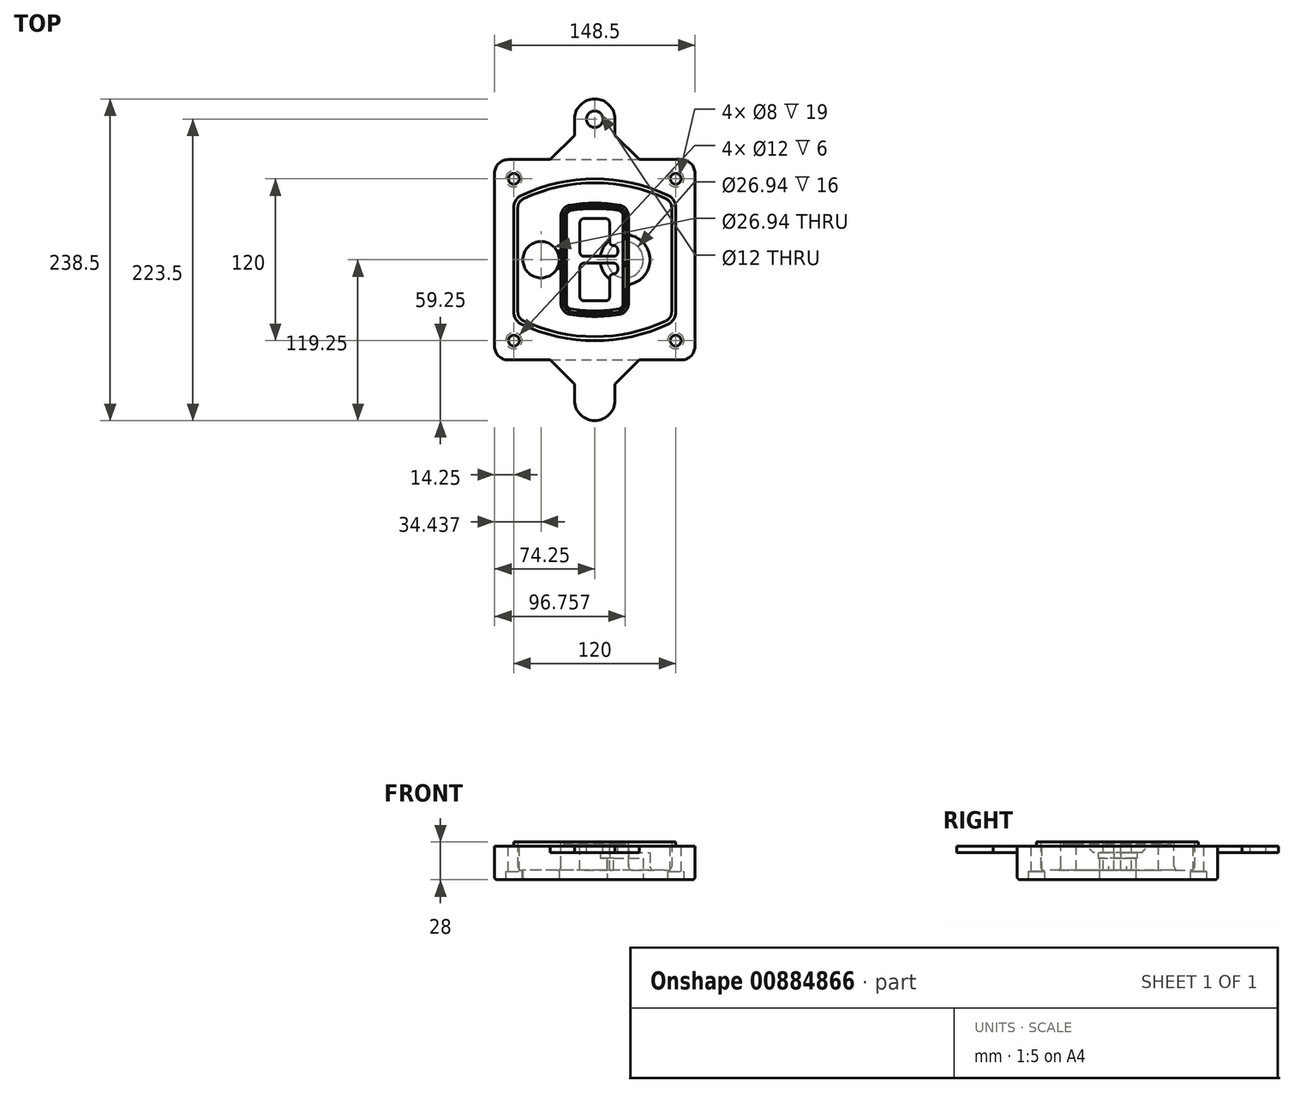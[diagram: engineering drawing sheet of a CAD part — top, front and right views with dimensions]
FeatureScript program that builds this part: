
annotation { "Feature Type Name" : "Feature", "Feature Type Description" : "" }
export const myFeature = defineFeature(function(context is Context, id is Id, definition is map)
    precondition{}
    {
        {
            var Q0;
            Q0=qCreatedBy(makeId("Top.planeOp"),FACE);
            var sketch = newSketch(context, id + "F0", { "sketchPlane" : qUnion([Q0])});
            skPoint(sketch, "E0.rect.middle", {"position": v(0, 0) * mm});
            skLineSegment(sketch, "E1.bottom", {"start": v(-64.25, -74.25) * mm, "end": v(64.25, -74.25) * mm});
            skLineSegment(sketch, "E1.top", {"start": v(-64.25, 74.25) * mm, "end": v(64.25, 74.25) * mm});
            skLineSegment(sketch, "E1.left", {"start": v(-74.25, -64.25) * mm, "end": v(-74.25, 64.25) * mm});
            skLineSegment(sketch, "E1.right", {"start": v(74.25, -64.25) * mm, "end": v(74.25, 64.25) * mm});
            skLineSegment(sketch, "E2", {"start": v(-74.25, 74.25) * mm, "end": v(74.25, -74.25) * mm, "construction": true});
            skLineSegment(sketch, "E3", {"start": v(74.25, 74.25) * mm, "end": v(-74.25, -74.25) * mm, "construction": true});
            skCircle(sketch, "E4", {"center": v(-60, 60) * mm, "radius": 4 * mm});
            skCircle(sketch, "E5", {"center": v(60, 60) * mm, "radius": 4 * mm});
            skCircle(sketch, "E6", {"center": v(60, -60) * mm, "radius": 4 * mm});
            skCircle(sketch, "E7", {"center": v(-60, -60) * mm, "radius": 4 * mm});
            skLineSegment(sketch, "E8", {"start": v(-60, 60) * mm, "end": v(60, 60) * mm, "construction": true});
            skLineSegment(sketch, "E9", {"start": v(60, 60) * mm, "end": v(60, -60) * mm, "construction": true});
            skLineSegment(sketch, "E10", {"start": v(60, -60) * mm, "end": v(-60, -60) * mm, "construction": true});
            skLineSegment(sketch, "E11", {"start": v(-60, -60) * mm, "end": v(-60, 60) * mm, "construction": true});
            skLineSegment(sketch, "E12", {"start": v(-60, 38.83) * mm, "end": v(-60, -38.83) * mm});
            skLineSegment(sketch, "E13", {"start": v(60, 38.83) * mm, "end": v(60, -38.83) * mm});
            skArc(sketch, "E14", {"start": v(54.26, 47.88) * mm, "mid": v(0, 60) * mm, "end": v(-54.26, 47.88) * mm});
            skArc(sketch, "E15", {"start": v(-54.26, -47.88) * mm, "mid": v(0, -60) * mm, "end": v(54.26, -47.88) * mm});
            skLineSegment(sketch, "E16", {"start": v(-60, 0) * mm, "end": v(60, 0) * mm, "construction": true});
            skPoint(sketch, "E17.visualSharp", {"position": v(-60, -45) * mm});
            skArc(sketch, "E17.filletArc", {"start": v(-60, -38.83) * mm, "mid": v(-58.44, -44.2) * mm, "end": v(-54.26, -47.88) * mm});
            skPoint(sketch, "E18.visualSharp", {"position": v(-60, 45) * mm});
            skArc(sketch, "E18.filletArc", {"start": v(-54.26, 47.88) * mm, "mid": v(-58.44, 44.2) * mm, "end": v(-60, 38.83) * mm});
            skPoint(sketch, "E19.visualSharp", {"position": v(60, 45) * mm});
            skArc(sketch, "E19.filletArc", {"start": v(60, 38.83) * mm, "mid": v(58.44, 44.2) * mm, "end": v(54.26, 47.88) * mm});
            skPoint(sketch, "E20.visualSharp", {"position": v(60, -45) * mm});
            skArc(sketch, "E20.filletArc", {"start": v(54.26, -47.88) * mm, "mid": v(58.44, -44.2) * mm, "end": v(60, -38.83) * mm});
            skPoint(sketch, "E21.visualSharp", {"position": v(-74.25, 74.25) * mm});
            skArc(sketch, "E21.filletArc", {"start": v(-64.25, 74.25) * mm, "mid": v(-71.32, 71.32) * mm, "end": v(-74.25, 64.25) * mm});
            skPoint(sketch, "E22.visualSharp", {"position": v(74.25, 74.25) * mm});
            skArc(sketch, "E22.filletArc", {"start": v(74.25, 64.25) * mm, "mid": v(71.32, 71.32) * mm, "end": v(64.25, 74.25) * mm});
            skPoint(sketch, "E23.visualSharp", {"position": v(74.25, -74.25) * mm});
            skArc(sketch, "E23.filletArc", {"start": v(64.25, -74.25) * mm, "mid": v(71.32, -71.32) * mm, "end": v(74.25, -64.25) * mm});
            skPoint(sketch, "E24.visualSharp", {"position": v(-74.25, -74.25) * mm});
            skArc(sketch, "E24.filletArc", {"start": v(-74.25, -64.25) * mm, "mid": v(-71.32, -71.32) * mm, "end": v(-64.25, -74.25) * mm});
            skArc(sketch, "E25.0", {"start": v(57, 38.83) * mm, "mid": v(55.9, 42.58) * mm, "end": v(52.98, 45.17) * mm});
            skLineSegment(sketch, "E25.1", {"start": v(57, 38.83) * mm, "end": v(57, -38.83) * mm});
            skArc(sketch, "E25.2", {"start": v(52.98, -45.17) * mm, "mid": v(55.9, -42.58) * mm, "end": v(57, -38.83) * mm});
            skArc(sketch, "E25.3", {"start": v(-52.98, -45.17) * mm, "mid": v(0, -57) * mm, "end": v(52.98, -45.17) * mm});
            skArc(sketch, "E25.4", {"start": v(-57, -38.83) * mm, "mid": v(-55.9, -42.58) * mm, "end": v(-52.98, -45.17) * mm});
            skArc(sketch, "E25.5", {"start": v(52.98, 45.17) * mm, "mid": v(0, 57) * mm, "end": v(-52.98, 45.17) * mm});
            skLineSegment(sketch, "E25.6", {"start": v(-57, 38.83) * mm, "end": v(-57, -38.83) * mm});
            skArc(sketch, "E25.7", {"start": v(-52.98, 45.17) * mm, "mid": v(-55.9, 42.58) * mm, "end": v(-57, 38.83) * mm});
            skArc(sketch, "E26.0", {"start": v(-55.96, 51.5) * mm, "mid": v(-61.82, 46.33) * mm, "end": v(-64, 38.83) * mm});
            skArc(sketch, "E26.1", {"start": v(55.96, 51.5) * mm, "mid": v(0, 64) * mm, "end": v(-55.96, 51.5) * mm});
            skArc(sketch, "E26.2", {"start": v(64, 38.83) * mm, "mid": v(61.82, 46.33) * mm, "end": v(55.96, 51.5) * mm});
            skLineSegment(sketch, "E26.3", {"start": v(64, 38.83) * mm, "end": v(64, -38.83) * mm});
            skArc(sketch, "E26.4", {"start": v(55.96, -51.5) * mm, "mid": v(61.82, -46.33) * mm, "end": v(64, -38.83) * mm});
            skLineSegment(sketch, "E26.5", {"start": v(-64, 38.83) * mm, "end": v(-64, -38.83) * mm});
            skArc(sketch, "E26.6", {"start": v(-55.96, -51.5) * mm, "mid": v(0, -64) * mm, "end": v(55.96, -51.5) * mm});
            skArc(sketch, "E26.7", {"start": v(-64, -38.83) * mm, "mid": v(-61.82, -46.33) * mm, "end": v(-55.96, -51.5) * mm});
            skSolve(sketch);
        }
        {
            var Q0;
            Q0=makeQuery(id+"F0.imprint","IMPRINT",FACE,{"disambiguationData":[TD([[makeQuery(id+"F0.imprint","IMPRINT",EDGE,{"derivedFrom":sQuery(id+"F0.wireOp",EDGE,"E1.bottom")}),1.0]])]});
            var Q1;
            Q1=makeQuery(id+"F0.imprint","IMPRINT",FACE,{"disambiguationData":[TD([[makeQuery(id+"F0.imprint","IMPRINT",EDGE,{"derivedFrom":sQuery(id+"F0.wireOp",EDGE,"E12")}),1.0]])]});
            var Q2;
            Q2=makeQuery(id+"F0.imprint","IMPRINT",FACE,{"disambiguationData":[TD([[makeQuery(id+"F0.imprint","IMPRINT",EDGE,{"derivedFrom":sQuery(id+"F0.wireOp",EDGE,"E25.0")}),1.0]])]});
            var Q3;
            Q3=makeQuery(id+"F0.imprint","IMPRINT",FACE,{"disambiguationData":[TD([[makeQuery(id+"F0.imprint","IMPRINT",EDGE,{"derivedFrom":sQuery(id+"F0.wireOp",EDGE,"E12")}),-1.0]])]});
            extrude(context, id + "F1", {"entities" : qUnion([Q0, Q1, Q2, Q3]), "oppositeDirection" : true, "depth" : 25 * mm});
        }
        {
            var Q0;
            Q0=makeQuery(id+"F0.imprint","IMPRINT",FACE,{"disambiguationData":[TD([[makeQuery(id+"F0.imprint","IMPRINT",EDGE,{"derivedFrom":sQuery(id+"F0.wireOp",EDGE,"E12")}),1.0]])]});
            extrude(context, id + "F2", {"entities" : qUnion([Q0]), "operationType" : NewBodyOperationType.ADD, "depth" : 3 * mm});
        }
        {
            var Q0;
            Q0=makeQuery(id+"F0.imprint","IMPRINT",FACE,{"disambiguationData":[TD([[makeQuery(id+"F0.imprint","IMPRINT",EDGE,{"derivedFrom":sQuery(id+"F0.wireOp",EDGE,"E25.0")}),1.0]])]});
            extrude(context, id + "F3", {"entities" : qUnion([Q0]), "operationType" : NewBodyOperationType.REMOVE, "oppositeDirection" : true, "depth" : 18 * mm});
        }
        {
            var Q0;
            Q0=makeQuery(id+"F2.opExtrude","CAP_FACE",FACE,{"disambiguationData":[OSD([sQuery(id+"F0.wireOp",EDGE,"E12"),sQuery(id+"F0.wireOp",EDGE,"E13"),sQuery(id+"F0.wireOp",EDGE,"E14"),sQuery(id+"F0.wireOp",EDGE,"E15"),sQuery(id+"F0.wireOp",EDGE,"E17.filletArc"),sQuery(id+"F0.wireOp",EDGE,"E18.filletArc"),sQuery(id+"F0.wireOp",EDGE,"E19.filletArc"),sQuery(id+"F0.wireOp",EDGE,"E20.filletArc"),sQuery(id+"F0.wireOp",EDGE,"E25.0"),sQuery(id+"F0.wireOp",EDGE,"E25.1"),sQuery(id+"F0.wireOp",EDGE,"E25.2"),sQuery(id+"F0.wireOp",EDGE,"E25.3"),sQuery(id+"F0.wireOp",EDGE,"E25.4"),sQuery(id+"F0.wireOp",EDGE,"E25.5"),sQuery(id+"F0.wireOp",EDGE,"E25.6"),sQuery(id+"F0.wireOp",EDGE,"E25.7")])],"isStart":false});
            var sketch = newSketch(context, id + "F4", { "sketchPlane" : qUnion([Q0])});
            skArc(sketch, "E27.0", {"start": v(-18.34, -40.45) * mm, "mid": v(0, -42) * mm, "end": v(18.34, -40.45) * mm});
            skArc(sketch, "E28.0", {"start": v(18.34, 40.45) * mm, "mid": v(0, 42) * mm, "end": v(-18.34, 40.45) * mm});
            skLineSegment(sketch, "E29", {"start": v(-25, 32.57) * mm, "end": v(-25, -32.57) * mm});
            skLineSegment(sketch, "E30", {"start": v(25, 32.57) * mm, "end": v(25, -32.57) * mm});
            skLineSegment(sketch, "E31", {"start": v(-25, 39.1) * mm, "end": v(25, 39.1) * mm, "construction": true});
            skLineSegment(sketch, "E32", {"start": v(-25, -39.1) * mm, "end": v(25, -39.1) * mm, "construction": true});
            skPoint(sketch, "E33.visualSharp", {"position": v(-25, 39.1) * mm});
            skArc(sketch, "E33.filletArc", {"start": v(-18.34, 40.45) * mm, "mid": v(-23.11, 37.73) * mm, "end": v(-25, 32.57) * mm});
            skPoint(sketch, "E34.visualSharp", {"position": v(25, 39.1) * mm});
            skArc(sketch, "E34.filletArc", {"start": v(25, 32.57) * mm, "mid": v(23.11, 37.73) * mm, "end": v(18.34, 40.45) * mm});
            skPoint(sketch, "E35.visualSharp", {"position": v(25, -39.1) * mm});
            skArc(sketch, "E35.filletArc", {"start": v(18.34, -40.45) * mm, "mid": v(23.11, -37.73) * mm, "end": v(25, -32.57) * mm});
            skPoint(sketch, "E36.visualSharp", {"position": v(-25, -39.1) * mm});
            skArc(sketch, "E36.filletArc", {"start": v(-25, -32.57) * mm, "mid": v(-23.11, -37.73) * mm, "end": v(-18.34, -40.45) * mm});
            skArc(sketch, "E37.0", {"start": v(52.98, 45.17) * mm, "mid": v(0, 57) * mm, "end": v(-52.98, 45.17) * mm});
            skArc(sketch, "E37.1", {"start": v(-52.98, 45.17) * mm, "mid": v(-55.9, 42.58) * mm, "end": v(-57, 38.83) * mm});
            skLineSegment(sketch, "E37.2", {"start": v(-57, 38.83) * mm, "end": v(-57, -38.83) * mm});
            skArc(sketch, "E37.3", {"start": v(-57, -38.83) * mm, "mid": v(-55.9, -42.58) * mm, "end": v(-52.98, -45.17) * mm});
            skArc(sketch, "E37.4", {"start": v(-52.98, -45.17) * mm, "mid": v(0, -57) * mm, "end": v(52.98, -45.17) * mm});
            skArc(sketch, "E37.5", {"start": v(52.98, -45.17) * mm, "mid": v(55.9, -42.58) * mm, "end": v(57, -38.83) * mm});
            skLineSegment(sketch, "E37.6", {"start": v(57, 38.83) * mm, "end": v(57, -38.83) * mm});
            skArc(sketch, "E37.7", {"start": v(57, 38.83) * mm, "mid": v(55.9, 42.58) * mm, "end": v(52.98, 45.17) * mm});
            skLineSegment(sketch, "E38.0", {"start": v(23, 32.57) * mm, "end": v(23, -32.57) * mm});
            skArc(sketch, "E38.1", {"start": v(18, -38.48) * mm, "mid": v(21.58, -36.44) * mm, "end": v(23, -32.57) * mm});
            skArc(sketch, "E38.2", {"start": v(-18, -38.48) * mm, "mid": v(0, -40) * mm, "end": v(18, -38.48) * mm});
            skArc(sketch, "E38.3", {"start": v(-23, -32.57) * mm, "mid": v(-21.58, -36.44) * mm, "end": v(-18, -38.48) * mm});
            skLineSegment(sketch, "E38.4", {"start": v(-23, 32.57) * mm, "end": v(-23, -32.57) * mm});
            skArc(sketch, "E38.5", {"start": v(23, 32.57) * mm, "mid": v(21.58, 36.44) * mm, "end": v(18, 38.48) * mm});
            skArc(sketch, "E38.6", {"start": v(-18, 38.48) * mm, "mid": v(-21.58, 36.44) * mm, "end": v(-23, 32.57) * mm});
            skArc(sketch, "E38.7", {"start": v(18, 38.48) * mm, "mid": v(0, 40) * mm, "end": v(-18, 38.48) * mm});
            skArc(sketch, "E39.0", {"start": v(21, 32.57) * mm, "mid": v(20.06, 35.15) * mm, "end": v(17.67, 36.5) * mm});
            skLineSegment(sketch, "E39.1", {"start": v(21, 32.57) * mm, "end": v(21, -32.57) * mm});
            skArc(sketch, "E39.2", {"start": v(17.67, -36.5) * mm, "mid": v(20.06, -35.15) * mm, "end": v(21, -32.57) * mm});
            skArc(sketch, "E39.3", {"start": v(-17.67, -36.5) * mm, "mid": v(0, -38) * mm, "end": v(17.67, -36.5) * mm});
            skArc(sketch, "E39.4", {"start": v(-21, -32.57) * mm, "mid": v(-20.06, -35.15) * mm, "end": v(-17.67, -36.5) * mm});
            skArc(sketch, "E39.5", {"start": v(17.67, 36.5) * mm, "mid": v(0, 38) * mm, "end": v(-17.67, 36.5) * mm});
            skLineSegment(sketch, "E39.6", {"start": v(-21, 32.57) * mm, "end": v(-21, -32.57) * mm});
            skArc(sketch, "E39.7", {"start": v(-17.67, 36.5) * mm, "mid": v(-20.06, 35.15) * mm, "end": v(-21, 32.57) * mm});
            skLineSegment(sketch, "E40", {"start": v(-25, 0) * mm, "end": v(25, 0) * mm, "construction": true});
            skLineSegment(sketch, "E41", {"start": v(-11, 5.5) * mm, "end": v(-11, 27.5) * mm});
            skLineSegment(sketch, "E42", {"start": v(-8, 30.5) * mm, "end": v(8, 30.5) * mm});
            skLineSegment(sketch, "E43", {"start": v(11, 27.5) * mm, "end": v(11, 13.5) * mm});
            skLineSegment(sketch, "E44", {"start": v(14, 10.5) * mm, "end": v(14, 10.5) * mm});
            skLineSegment(sketch, "E45", {"start": v(17, 7.5) * mm, "end": v(17, 5.5) * mm});
            skLineSegment(sketch, "E46", {"start": v(14, 2.5) * mm, "end": v(-8, 2.5) * mm});
            skPoint(sketch, "E47.visualSharp", {"position": v(-11, 30.5) * mm});
            skArc(sketch, "E47.filletArc", {"start": v(-8, 30.5) * mm, "mid": v(-10.12, 29.62) * mm, "end": v(-11, 27.5) * mm});
            skPoint(sketch, "E48.visualSharp", {"position": v(11, 30.5) * mm});
            skArc(sketch, "E48.filletArc", {"start": v(11, 27.5) * mm, "mid": v(10.12, 29.62) * mm, "end": v(8, 30.5) * mm});
            skPoint(sketch, "E49.visualSharp", {"position": v(11, 10.5) * mm});
            skArc(sketch, "E49.filletArc", {"start": v(11, 13.5) * mm, "mid": v(11.88, 11.38) * mm, "end": v(14, 10.5) * mm});
            skPoint(sketch, "E50.visualSharp", {"position": v(17, 10.5) * mm});
            skArc(sketch, "E50.filletArc", {"start": v(17, 7.5) * mm, "mid": v(16.12, 9.62) * mm, "end": v(14, 10.5) * mm});
            skPoint(sketch, "E51.visualSharp", {"position": v(17, 2.5) * mm});
            skArc(sketch, "E51.filletArc", {"start": v(14, 2.5) * mm, "mid": v(16.12, 3.38) * mm, "end": v(17, 5.5) * mm});
            skPoint(sketch, "E52.visualSharp", {"position": v(-11, 2.5) * mm});
            skArc(sketch, "E52.filletArc", {"start": v(-11, 5.5) * mm, "mid": v(-10.12, 3.38) * mm, "end": v(-8, 2.5) * mm});
            skLineSegment(sketch, "E53.0.MirrorCS", {"start": v(14, -2.5) * mm, "end": v(-8, -2.5) * mm});
            skArc(sketch, "E54.0.MirrorCS", {"start": v(-11, -5.5) * mm, "mid": v(-10.12, -3.38) * mm, "end": v(-8, -2.5) * mm});
            skLineSegment(sketch, "E55.0.MirrorCS", {"start": v(-11, -5.5) * mm, "end": v(-11, -27.5) * mm});
            skArc(sketch, "E56.0.MirrorCS", {"start": v(-8, -30.5) * mm, "mid": v(-10.12, -29.62) * mm, "end": v(-11, -27.5) * mm});
            skLineSegment(sketch, "E57.0.MirrorCS", {"start": v(-8, -30.5) * mm, "end": v(8, -30.5) * mm});
            skArc(sketch, "E58.0.MirrorCS", {"start": v(11, -27.5) * mm, "mid": v(10.12, -29.62) * mm, "end": v(8, -30.5) * mm});
            skLineSegment(sketch, "E59.0.MirrorCS", {"start": v(11, -27.5) * mm, "end": v(11, -13.5) * mm});
            skArc(sketch, "E60.0.MirrorCS", {"start": v(11, -13.5) * mm, "mid": v(11.88, -11.38) * mm, "end": v(14, -10.5) * mm});
            skArc(sketch, "E61.0.MirrorCS", {"start": v(17, -7.5) * mm, "mid": v(16.12, -9.62) * mm, "end": v(14, -10.5) * mm});
            skLineSegment(sketch, "E62.0.MirrorCS", {"start": v(17, -7.5) * mm, "end": v(17, -5.5) * mm});
            skArc(sketch, "E63.0.MirrorCS", {"start": v(14, -2.5) * mm, "mid": v(16.12, -3.38) * mm, "end": v(17, -5.5) * mm});
            skSolve(sketch);
        }
        {
            var Q0;
            Q0=makeQuery(id+"F4.imprint","IMPRINT",FACE,{"disambiguationData":[TD([[makeQuery(id+"F4.imprint","IMPRINT",EDGE,{"derivedFrom":sQuery(id+"F4.wireOp",EDGE,"E27.0")}),1.0]])]});
            var Q1;
            Q1=makeQuery(id+"F4.imprint","IMPRINT",FACE,{"disambiguationData":[TD([[makeQuery(id+"F4.imprint","IMPRINT",EDGE,{"derivedFrom":sQuery(id+"F4.wireOp",EDGE,"E38.0")}),-1.0]])]});
            var Q2;
            Q2=makeQuery(id+"F4.imprint","IMPRINT",FACE,{"disambiguationData":[TD([[makeQuery(id+"F4.imprint","IMPRINT",EDGE,{"derivedFrom":sQuery(id+"F4.wireOp",EDGE,"E39.0")}),1.0]])]});
            extrude(context, id + "F5", {"entities" : qUnion([Q0, Q1, Q2]), "operationType" : NewBodyOperationType.ADD, "endBound" : BoundingType.UP_TO_NEXT, "oppositeDirection" : true, "depth" : 25 * mm});
        }
        {
            var Q0;
            Q0=makeQuery(id+"F4.imprint","IMPRINT",FACE,{"disambiguationData":[TD([[makeQuery(id+"F4.imprint","IMPRINT",EDGE,{"derivedFrom":sQuery(id+"F4.wireOp",EDGE,"E38.0")}),-1.0]])]});
            extrude(context, id + "F6", {"entities" : qUnion([Q0]), "operationType" : NewBodyOperationType.REMOVE, "oppositeDirection" : true, "depth" : 2 * mm});
        }
        {
            var Q0;
            Q0=makeQuery(id+"F1.opExtrude","CAP_FACE",FACE,{"disambiguationData":[OSD([sQuery(id+"F0.wireOp",EDGE,"E1.bottom"),sQuery(id+"F0.wireOp",EDGE,"E1.top"),sQuery(id+"F0.wireOp",EDGE,"E1.left"),sQuery(id+"F0.wireOp",EDGE,"E1.right"),sQuery(id+"F0.wireOp",EDGE,"E4"),sQuery(id+"F0.wireOp",EDGE,"E5"),sQuery(id+"F0.wireOp",EDGE,"E6"),sQuery(id+"F0.wireOp",EDGE,"E7"),sQuery(id+"F0.wireOp",EDGE,"E21.filletArc"),sQuery(id+"F0.wireOp",EDGE,"E22.filletArc"),sQuery(id+"F0.wireOp",EDGE,"E23.filletArc"),sQuery(id+"F0.wireOp",EDGE,"E24.filletArc")])],"isStart":false});
            var sketch = newSketch(context, id + "F7", { "sketchPlane" : qUnion([Q0])});
            skCircle(sketch, "E64", {"center": v(22.5, 0) * mm, "radius": 13.47 * mm});
            skCircle(sketch, "E65", {"center": v(-39.81, 0) * mm, "radius": 13.47 * mm});
            skLineSegment(sketch, "E66", {"start": v(74.25, 0) * mm, "end": v(-74.25, 0) * mm});
            skCircle(sketch, "E67", {"center": v(22.5, 0) * mm, "radius": 18.47 * mm});
            skCircle(sketch, "E68", {"center": v(60, -60) * mm, "radius": 6 * mm});
            skCircle(sketch, "E69", {"center": v(-60, -60) * mm, "radius": 6 * mm});
            skCircle(sketch, "E70", {"center": v(-60, 60) * mm, "radius": 6 * mm});
            skCircle(sketch, "E71", {"center": v(60, 60) * mm, "radius": 6 * mm});
            skSolve(sketch);
        }
        {
            var Q0;
            {var subQ1=sQuery(id+"F7.wireOp",EDGE,"E66");var subQ4=sQuery(id+"F7.wireOp",EDGE,"E64");var subQ6=makeQuery(id+"F7.imprint","INTERSECT",VERTEX,{"disambiguationData":[OD(0.0)],"derivedFrom":[subQ4,subQ1]});Q0=makeQuery(id+"F7.imprint","IMPRINT",FACE,{"disambiguationData":[TD([[makeQuery(id+"F7.imprint","IMPRINT",EDGE,{"disambiguationData":[TD([[subQ6,-1.0]])],"derivedFrom":subQ4}),-1.0]])]});}
            var Q1;
            {var subQ0=sQuery(id+"F7.wireOp",EDGE,"E66");var subQ1=sQuery(id+"F7.wireOp",EDGE,"E64");var subQ3=makeQuery(id+"F7.imprint","INTERSECT",VERTEX,{"disambiguationData":[OD(0.0)],"derivedFrom":[subQ1,subQ0]});Q1=makeQuery(id+"F7.imprint","IMPRINT",FACE,{"disambiguationData":[TD([[makeQuery(id+"F7.imprint","IMPRINT",EDGE,{"disambiguationData":[TD([[subQ3,-1.0]])],"derivedFrom":subQ1}),1.0]])]});}
            var Q2;
            {var subQ0=sQuery(id+"F7.wireOp",EDGE,"E66");var subQ1=sQuery(id+"F7.wireOp",EDGE,"E64");var subQ3=makeQuery(id+"F7.imprint","INTERSECT",VERTEX,{"disambiguationData":[OD(0.0)],"derivedFrom":[subQ1,subQ0]});Q2=makeQuery(id+"F7.imprint","IMPRINT",FACE,{"disambiguationData":[TD([[makeQuery(id+"F7.imprint","IMPRINT",EDGE,{"disambiguationData":[TD([[subQ3,1.0]])],"derivedFrom":subQ1}),1.0]])]});}
            var Q3;
            {var subQ1=sQuery(id+"F7.wireOp",EDGE,"E66");var subQ4=sQuery(id+"F7.wireOp",EDGE,"E64");var subQ6=makeQuery(id+"F7.imprint","INTERSECT",VERTEX,{"disambiguationData":[OD(0.0)],"derivedFrom":[subQ4,subQ1]});Q3=makeQuery(id+"F7.imprint","IMPRINT",FACE,{"disambiguationData":[TD([[makeQuery(id+"F7.imprint","IMPRINT",EDGE,{"disambiguationData":[TD([[subQ6,1.0]])],"derivedFrom":subQ4}),-1.0]])]});}
            extrude(context, id + "F8", {"entities" : qUnion([Q0, Q1, Q2, Q3]), "operationType" : NewBodyOperationType.ADD, "oppositeDirection" : true, "depth" : 20 * mm});
        }
        {
            var Q0;
            {var subQ0=sQuery(id+"F7.wireOp",EDGE,"E66");var subQ1=sQuery(id+"F7.wireOp",EDGE,"E64");var subQ3=makeQuery(id+"F7.imprint","INTERSECT",VERTEX,{"disambiguationData":[OD(0.0)],"derivedFrom":[subQ1,subQ0]});Q0=makeQuery(id+"F7.imprint","IMPRINT",FACE,{"disambiguationData":[TD([[makeQuery(id+"F7.imprint","IMPRINT",EDGE,{"disambiguationData":[TD([[subQ3,-1.0]])],"derivedFrom":subQ1}),1.0]])]});}
            var Q1;
            {var subQ0=sQuery(id+"F7.wireOp",EDGE,"E66");var subQ1=sQuery(id+"F7.wireOp",EDGE,"E64");var subQ3=makeQuery(id+"F7.imprint","INTERSECT",VERTEX,{"disambiguationData":[OD(0.0)],"derivedFrom":[subQ1,subQ0]});Q1=makeQuery(id+"F7.imprint","IMPRINT",FACE,{"disambiguationData":[TD([[makeQuery(id+"F7.imprint","IMPRINT",EDGE,{"disambiguationData":[TD([[subQ3,1.0]])],"derivedFrom":subQ1}),1.0]])]});}
            extrude(context, id + "F9", {"entities" : qUnion([Q0, Q1]), "operationType" : NewBodyOperationType.REMOVE, "oppositeDirection" : true, "depth" : 16 * mm});
        }
        {
            var Q0;
            {var subQ0=sQuery(id+"F7.wireOp",EDGE,"E66");var subQ1=sQuery(id+"F7.wireOp",EDGE,"E65");var subQ3=makeQuery(id+"F7.imprint","INTERSECT",VERTEX,{"disambiguationData":[OD(0.0)],"derivedFrom":[subQ1,subQ0]});Q0=makeQuery(id+"F7.imprint","IMPRINT",FACE,{"disambiguationData":[TD([[makeQuery(id+"F7.imprint","IMPRINT",EDGE,{"disambiguationData":[TD([[subQ3,-1.0]])],"derivedFrom":subQ1}),1.0]])]});}
            var Q1;
            {var subQ0=sQuery(id+"F7.wireOp",EDGE,"E66");var subQ1=sQuery(id+"F7.wireOp",EDGE,"E65");var subQ3=makeQuery(id+"F7.imprint","INTERSECT",VERTEX,{"disambiguationData":[OD(0.0)],"derivedFrom":[subQ1,subQ0]});Q1=makeQuery(id+"F7.imprint","IMPRINT",FACE,{"disambiguationData":[TD([[makeQuery(id+"F7.imprint","IMPRINT",EDGE,{"disambiguationData":[TD([[subQ3,1.0]])],"derivedFrom":subQ1}),1.0]])]});}
            extrude(context, id + "F10", {"entities" : qUnion([Q0, Q1]), "operationType" : NewBodyOperationType.REMOVE, "oppositeDirection" : true, "depth" : 25 * mm});
        }
        {
            var Q0;
            Q0=makeQuery(id+"F7.imprint","IMPRINT",FACE,{"disambiguationData":[TD([[makeQuery(id+"F7.imprint","IMPRINT",EDGE,{"derivedFrom":sQuery(id+"F7.wireOp",EDGE,"E68")}),1.0]])]});
            var Q1;
            Q1=makeQuery(id+"F7.imprint","IMPRINT",FACE,{"disambiguationData":[TD([[makeQuery(id+"F7.imprint","IMPRINT",EDGE,{"derivedFrom":makeQuery(id+"F1.opExtrude","CAP_EDGE",EDGE,{"disambiguationData":[OSD([sQuery(id+"F0.wireOp",EDGE,"E5")])],"isStart":false})}),-1.0]])]});
            var Q2;
            Q2=makeQuery(id+"F7.imprint","IMPRINT",FACE,{"disambiguationData":[TD([[makeQuery(id+"F7.imprint","IMPRINT",EDGE,{"derivedFrom":sQuery(id+"F7.wireOp",EDGE,"E69")}),1.0]])]});
            var Q3;
            Q3=makeQuery(id+"F7.imprint","IMPRINT",FACE,{"disambiguationData":[TD([[makeQuery(id+"F7.imprint","IMPRINT",EDGE,{"derivedFrom":makeQuery(id+"F1.opExtrude","CAP_EDGE",EDGE,{"disambiguationData":[OSD([sQuery(id+"F0.wireOp",EDGE,"E4")])],"isStart":false})}),-1.0]])]});
            var Q4;
            Q4=makeQuery(id+"F7.imprint","IMPRINT",FACE,{"disambiguationData":[TD([[makeQuery(id+"F7.imprint","IMPRINT",EDGE,{"derivedFrom":sQuery(id+"F7.wireOp",EDGE,"E70")}),1.0]])]});
            var Q5;
            Q5=makeQuery(id+"F7.imprint","IMPRINT",FACE,{"disambiguationData":[TD([[makeQuery(id+"F7.imprint","IMPRINT",EDGE,{"derivedFrom":makeQuery(id+"F1.opExtrude","CAP_EDGE",EDGE,{"disambiguationData":[OSD([sQuery(id+"F0.wireOp",EDGE,"E7")])],"isStart":false})}),-1.0]])]});
            var Q6;
            Q6=makeQuery(id+"F7.imprint","IMPRINT",FACE,{"disambiguationData":[TD([[makeQuery(id+"F7.imprint","IMPRINT",EDGE,{"derivedFrom":sQuery(id+"F7.wireOp",EDGE,"E71")}),1.0]])]});
            var Q7;
            Q7=makeQuery(id+"F7.imprint","IMPRINT",FACE,{"disambiguationData":[TD([[makeQuery(id+"F7.imprint","IMPRINT",EDGE,{"derivedFrom":makeQuery(id+"F1.opExtrude","CAP_EDGE",EDGE,{"disambiguationData":[OSD([sQuery(id+"F0.wireOp",EDGE,"E6")])],"isStart":false})}),-1.0]])]});
            extrude(context, id + "F11", {"entities" : qUnion([Q0, Q1, Q2, Q3, Q4, Q5, Q6, Q7]), "operationType" : NewBodyOperationType.REMOVE, "oppositeDirection" : true, "depth" : 6 * mm});
        }
        {
            var Q0;
            Q0=makeQuery(id+"F9.boolean.opBoolean","COPY",FACE,{"derivedFrom":makeQuery(id+"F9.opExtrude","CAP_FACE",FACE,{"disambiguationData":[OSD([sQuery(id+"F7.wireOp",EDGE,"E64")])],"isStart":false})});
            var sketch = newSketch(context, id + "F12", { "sketchPlane" : qUnion([Q0])});
            skArc(sketch, "E72.0", {"start": v(11, 14.45) * mm, "mid": v(6.45, 9.13) * mm, "end": v(4.2, 2.5) * mm});
            skArc(sketch, "E72.1", {"start": v(4.2, -2.5) * mm, "mid": v(6.45, -9.13) * mm, "end": v(11, -14.45) * mm});
            skLineSegment(sketch, "E73", {"start": v(4.2, -2.5) * mm, "end": v(14, -2.5) * mm});
            skLineSegment(sketch, "E74.0", {"start": v(14, 2.5) * mm, "end": v(4.2, 2.5) * mm});
            skArc(sketch, "E74.1", {"start": v(14, 2.5) * mm, "mid": v(16.12, 3.38) * mm, "end": v(17, 5.5) * mm});
            skLineSegment(sketch, "E74.2", {"start": v(17, 7.5) * mm, "end": v(17, 5.5) * mm});
            skArc(sketch, "E74.3", {"start": v(17, 7.5) * mm, "mid": v(16.12, 9.62) * mm, "end": v(14, 10.5) * mm});
            skArc(sketch, "E74.4", {"start": v(11, 13.5) * mm, "mid": v(11.88, 11.38) * mm, "end": v(14, 10.5) * mm});
            skLineSegment(sketch, "E74.5", {"start": v(11, 14.45) * mm, "end": v(11, 13.5) * mm});
            skLineSegment(sketch, "E74.7", {"start": v(14, -2.5) * mm, "end": v(4.2, -2.5) * mm});
            skArc(sketch, "E74.8", {"start": v(14, -2.5) * mm, "mid": v(16.12, -3.38) * mm, "end": v(17, -5.5) * mm});
            skLineSegment(sketch, "E74.9", {"start": v(17, -7.5) * mm, "end": v(17, -5.5) * mm});
            skArc(sketch, "E74.10", {"start": v(17, -7.5) * mm, "mid": v(16.12, -9.62) * mm, "end": v(14, -10.5) * mm});
            skArc(sketch, "E74.11", {"start": v(11, -13.5) * mm, "mid": v(11.88, -11.38) * mm, "end": v(14, -10.5) * mm});
            skLineSegment(sketch, "E74.12", {"start": v(11, -14.45) * mm, "end": v(11, -13.5) * mm});
            skPoint(sketch, "E75.orphan", {"position": v(11, -27.5) * mm});
            skPoint(sketch, "E76.orphan", {"position": v(-8, -2.5) * mm});
            skPoint(sketch, "E77.orphan", {"position": v(-8, 2.5) * mm});
            skPoint(sketch, "E78.orphan", {"position": v(11, 27.5) * mm});
            skSolve(sketch);
        }
        {
            var Q0;
            {var subQ7=sQuery(id+"F12.wireOp",EDGE,"E72.0");var subQ14=sQuery(id+"F12.wireOp",EDGE,"E72.1");var subQ16=sQuery(id+"F12.wireOp",EDGE,"E74.1");var subQ18=sQuery(id+"F12.wireOp",EDGE,"E74.8");Q0=qUnion([makeQuery(id+"F12.imprint","IMPRINT",FACE,{"disambiguationData":[TD([[makeQuery(id+"F12.imprint","IMPRINT",EDGE,{"derivedFrom":subQ7}),1.0]])]}),makeQuery(id+"F12.imprint","IMPRINT",FACE,{"disambiguationData":[TD([[makeQuery(id+"F12.imprint","IMPRINT",EDGE,{"derivedFrom":subQ14}),1.0]])]}),makeQuery(id+"F12.imprint","IMPRINT",FACE,{"disambiguationData":[TD([[makeQuery(id+"F12.imprint","IMPRINT",EDGE,{"derivedFrom":subQ16}),1.0]])]}),makeQuery(id+"F12.imprint","IMPRINT",FACE,{"disambiguationData":[TD([[makeQuery(id+"F12.imprint","IMPRINT",EDGE,{"derivedFrom":subQ18}),-1.0]])]})]);}
            var Q1;
            Q1=makeQuery(id+"F5.boolean.opBoolean","SPLIT",FACE,{"disambiguationData":[TD([makeQuery(id+"F5.opExtrude","SWEPT_FACE",FACE,{"disambiguationData":[OSD([sQuery(id+"F4.wireOp",EDGE,"E41")])]})])],"derivedFrom":makeQuery(id+"F3.boolean.opBoolean","COPY",FACE,{"derivedFrom":makeQuery(id+"F3.opExtrude","CAP_FACE",FACE,{"disambiguationData":[OSD([sQuery(id+"F0.wireOp",EDGE,"E25.0"),sQuery(id+"F0.wireOp",EDGE,"E25.1"),sQuery(id+"F0.wireOp",EDGE,"E25.2"),sQuery(id+"F0.wireOp",EDGE,"E25.3"),sQuery(id+"F0.wireOp",EDGE,"E25.4"),sQuery(id+"F0.wireOp",EDGE,"E25.5"),sQuery(id+"F0.wireOp",EDGE,"E25.6"),sQuery(id+"F0.wireOp",EDGE,"E25.7")])],"isStart":false})})});
            extrude(context, id + "F13", {"entities" : qUnion([Q0]), "operationType" : NewBodyOperationType.REMOVE, "endBound" : BoundingType.UP_TO_SURFACE, "endBoundEntityFace" : qUnion([Q1]), "depth" : 25 * mm});
        }
        {
            var Q0;
            Q0=makeQuery(id+"F3.boolean.opBoolean","COPY",EDGE,{"derivedFrom":makeQuery(id+"F3.opExtrude","CAP_EDGE",EDGE,{"disambiguationData":[OSD([sQuery(id+"F0.wireOp",EDGE,"E25.6")])],"isStart":false})});
            var Q1;
            Q1=makeQuery(id+"F8.boolean.opBoolean","INTERSECT",EDGE,{"derivedFrom":[makeQuery(id+"F5.opExtrude","SWEPT_FACE",FACE,{"disambiguationData":[OSD([sQuery(id+"F4.wireOp",EDGE,"E30")])]}),makeQuery(id+"F8.opExtrude","CAP_FACE",FACE,{"disambiguationData":[OSD([sQuery(id+"F7.wireOp",EDGE,"E67")])],"isStart":false})]});
            var Q2;
            Q2=makeQuery(id+"F8.boolean.opBoolean","INTERSECT",EDGE,{"disambiguationData":[OD(1.0)],"derivedFrom":[makeQuery(id+"F5.opExtrude","SWEPT_FACE",FACE,{"disambiguationData":[OSD([sQuery(id+"F4.wireOp",EDGE,"E30")])]}),makeQuery(id+"F8.opExtrude","SWEPT_FACE",FACE,{"disambiguationData":[OSD([sQuery(id+"F7.wireOp",EDGE,"E67")])]})]});
            var Q3;
            {var subQ0=sQuery(id+"F4.wireOp",EDGE,"E30");Q3=makeQuery(id+"F8.boolean.opBoolean","SPLIT",EDGE,{"disambiguationData":[TD([makeQuery(id+"F5.opExtrude","SWEPT_FACE",FACE,{"disambiguationData":[OSD([sQuery(id+"F4.wireOp",EDGE,"E35.filletArc")])]})])],"derivedFrom":makeQuery(id+"F5.opExtrude","CAP_EDGE",EDGE,{"disambiguationData":[OSD([subQ0])],"isStart":false})});}
            var Q4;
            {var subQ0=sQuery(id+"F0.wireOp",EDGE,"E25.7");var subQ1=sQuery(id+"F0.wireOp",EDGE,"E25.1");var subQ2=sQuery(id+"F0.wireOp",EDGE,"E25.6");var subQ3=sQuery(id+"F0.wireOp",EDGE,"E25.5");var subQ4=sQuery(id+"F0.wireOp",EDGE,"E25.4");var subQ5=sQuery(id+"F0.wireOp",EDGE,"E25.0");var subQ6=sQuery(id+"F0.wireOp",EDGE,"E25.2");var subQ7=sQuery(id+"F0.wireOp",EDGE,"E25.3");Q4=makeQuery(id+"F8.boolean.opBoolean","INTERSECT",EDGE,{"derivedFrom":[makeQuery(id+"F5.boolean.opBoolean","SPLIT",FACE,{"disambiguationData":[TD([makeQuery(id+"F2.opExtrude","SWEPT_FACE",FACE,{"disambiguationData":[OSD([subQ5])]})])],"derivedFrom":makeQuery(id+"F3.boolean.opBoolean","COPY",FACE,{"derivedFrom":makeQuery(id+"F3.opExtrude","CAP_FACE",FACE,{"disambiguationData":[OSD([subQ5,subQ1,subQ6,subQ7,subQ4,subQ3,subQ2,subQ0])],"isStart":false})})}),makeQuery(id+"F8.opExtrude","SWEPT_FACE",FACE,{"disambiguationData":[OSD([sQuery(id+"F7.wireOp",EDGE,"E67")])]})]});}
            var Q5;
            Q5=makeQuery(id+"F8.boolean.opBoolean","INTERSECT",EDGE,{"disambiguationData":[OD(0.0)],"derivedFrom":[makeQuery(id+"F5.opExtrude","SWEPT_FACE",FACE,{"disambiguationData":[OSD([sQuery(id+"F4.wireOp",EDGE,"E30")])]}),makeQuery(id+"F8.opExtrude","SWEPT_FACE",FACE,{"disambiguationData":[OSD([sQuery(id+"F7.wireOp",EDGE,"E67")])]})]});
            fillet(context, id + "F14", {"entities" : qUnion([Q0, Q1, Q2, Q3, Q4, Q5]), "radius" : 3 * mm, "tangentPropagation" : true, "allowEdgeOverflow" : false});
        }
        {
            var Q0;
            Q0=makeQuery(id+"F1.opExtrude","CAP_EDGE",EDGE,{"disambiguationData":[OSD([sQuery(id+"F0.wireOp",EDGE,"E1.bottom")])],"isStart":false});
            fillet(context, id + "F15", {"entities" : qUnion([Q0]), "radius" : 2 * mm, "tangentPropagation" : true, "allowEdgeOverflow" : false});
        }
        {
            var Q0;
            {var subQ0=sQuery(id+"F0.wireOp",EDGE,"E21.filletArc");var subQ1=sQuery(id+"F0.wireOp",EDGE,"E7");var subQ2=sQuery(id+"F0.wireOp",EDGE,"E6");var subQ3=sQuery(id+"F0.wireOp",EDGE,"E5");var subQ4=sQuery(id+"F0.wireOp",EDGE,"E4");var subQ5=sQuery(id+"F0.wireOp",EDGE,"E22.filletArc");var subQ6=sQuery(id+"F0.wireOp",EDGE,"E1.bottom");var subQ7=sQuery(id+"F0.wireOp",EDGE,"E1.right");var subQ8=sQuery(id+"F0.wireOp",EDGE,"E1.top");var subQ9=sQuery(id+"F0.wireOp",EDGE,"E1.left");var subQ10=sQuery(id+"F0.wireOp",EDGE,"E23.filletArc");var subQ11=sQuery(id+"F0.wireOp",EDGE,"E24.filletArc");Q0=makeQuery(id+"F2.boolean.opBoolean","SPLIT",FACE,{"disambiguationData":[TD([makeQuery(id+"F1.opExtrude","SWEPT_FACE",FACE,{"disambiguationData":[OSD([subQ6])]})])],"derivedFrom":makeQuery(id+"F1.opExtrude","CAP_FACE",FACE,{"disambiguationData":[OSD([subQ6,subQ8,subQ9,subQ7,subQ4,subQ3,subQ2,subQ1,subQ0,subQ5,subQ10,subQ11])],"isStart":true})});}
            var sketch = newSketch(context, id + "F16", { "sketchPlane" : qUnion([Q0])});
            skCircle(sketch, "E79", {"center": v(0, -104.25) * mm, "radius": 6 * mm});
            skArc(sketch, "E80", {"start": v(-15, -104.25) * mm, "mid": v(0, -119.25) * mm, "end": v(15, -104.25) * mm});
            skLineSegment(sketch, "E81.0", {"start": v(-15, -92.25) * mm, "end": v(-15, -104.25) * mm});
            skLineSegment(sketch, "E82.0", {"start": v(15, -92.25) * mm, "end": v(15, -104.25) * mm});
            skArc(sketch, "E83.0", {"start": v(52.13, -43.36) * mm, "mid": v(54.22, -41.51) * mm, "end": v(55, -38.83) * mm});
            skArc(sketch, "E83.1", {"start": v(-52.13, -43.36) * mm, "mid": v(0, -55) * mm, "end": v(52.13, -43.36) * mm});
            skLineSegment(sketch, "E83.2", {"start": v(55, -38.83) * mm, "end": v(55, 38.83) * mm});
            skArc(sketch, "E83.3", {"start": v(-55, -38.83) * mm, "mid": v(-54.22, -41.51) * mm, "end": v(-52.13, -43.36) * mm});
            skArc(sketch, "E83.4", {"start": v(55, 38.83) * mm, "mid": v(54.22, 41.51) * mm, "end": v(52.13, 43.36) * mm});
            skArc(sketch, "E83.5", {"start": v(52.13, 43.36) * mm, "mid": v(0, 55) * mm, "end": v(-52.13, 43.36) * mm});
            skArc(sketch, "E83.6", {"start": v(-52.13, 43.36) * mm, "mid": v(-54.22, 41.51) * mm, "end": v(-55, 38.83) * mm});
            skLineSegment(sketch, "E83.7", {"start": v(-55, 38.83) * mm, "end": v(-55, -38.83) * mm});
            skLineSegment(sketch, "E84", {"start": v(-15, -92.25) * mm, "end": v(-33, -74.25) * mm});
            skLineSegment(sketch, "E85.MirrorCS", {"start": v(15, -92.25) * mm, "end": v(33, -74.25) * mm});
            skLineSegment(sketch, "E86.MirrorCS", {"start": v(15, 92.25) * mm, "end": v(33, 74.25) * mm});
            skArc(sketch, "E87.MirrorCS", {"start": v(-15, 104.25) * mm, "mid": v(0, 119.25) * mm, "end": v(15, 104.25) * mm});
            skLineSegment(sketch, "E88.MirrorCS", {"start": v(-15, 92.25) * mm, "end": v(-33, 74.25) * mm});
            skLineSegment(sketch, "E89.MirrorCS", {"start": v(15, 92.25) * mm, "end": v(15, 104.25) * mm});
            skLineSegment(sketch, "E90.MirrorCS", {"start": v(-15, 92.25) * mm, "end": v(-15, 104.25) * mm});
            skCircle(sketch, "E91.MirrorC", {"center": v(0, 104.25) * mm, "radius": 6 * mm});
            skSolve(sketch);
        }
        {
            var Q0;
            Q0=makeQuery(id+"F16.imprint","IMPRINT",FACE,{"disambiguationData":[TD([[makeQuery(id+"F16.imprint","IMPRINT",EDGE,{"derivedFrom":sQuery(id+"F16.wireOp",EDGE,"E91.MirrorC")}),-1.0]])]});
            var Q1;
            {var subQ1=sQuery(id+"F16.wireOp",EDGE,"E86.MirrorCS");Q1=makeQuery(id+"F16.imprint","IMPRINT",FACE,{"disambiguationData":[TD([[makeQuery(id+"F16.imprint","IMPRINT",EDGE,{"derivedFrom":subQ1}),-1.0]])]});}
            var Q2;
            Q2=makeQuery(id+"F16.imprint","IMPRINT",FACE,{"disambiguationData":[TD([[makeQuery(id+"F16.imprint","IMPRINT",EDGE,{"derivedFrom":sQuery(id+"F16.wireOp",EDGE,"E79")}),-1.0]])]});
            var Q3;
            Q3=makeQuery(id+"F16.imprint","IMPRINT",FACE,{"disambiguationData":[TD([[makeQuery(id+"F16.imprint","IMPRINT",EDGE,{"derivedFrom":sQuery(id+"F16.wireOp",EDGE,"E79")}),1.0]])]});
            extrude(context, id + "F17", {"entities" : qUnion([Q0, Q1, Q2, Q3]), "operationType" : NewBodyOperationType.ADD, "depth" : -5 * mm, "offsetDistance" : 25 * mm});
        }
    });
